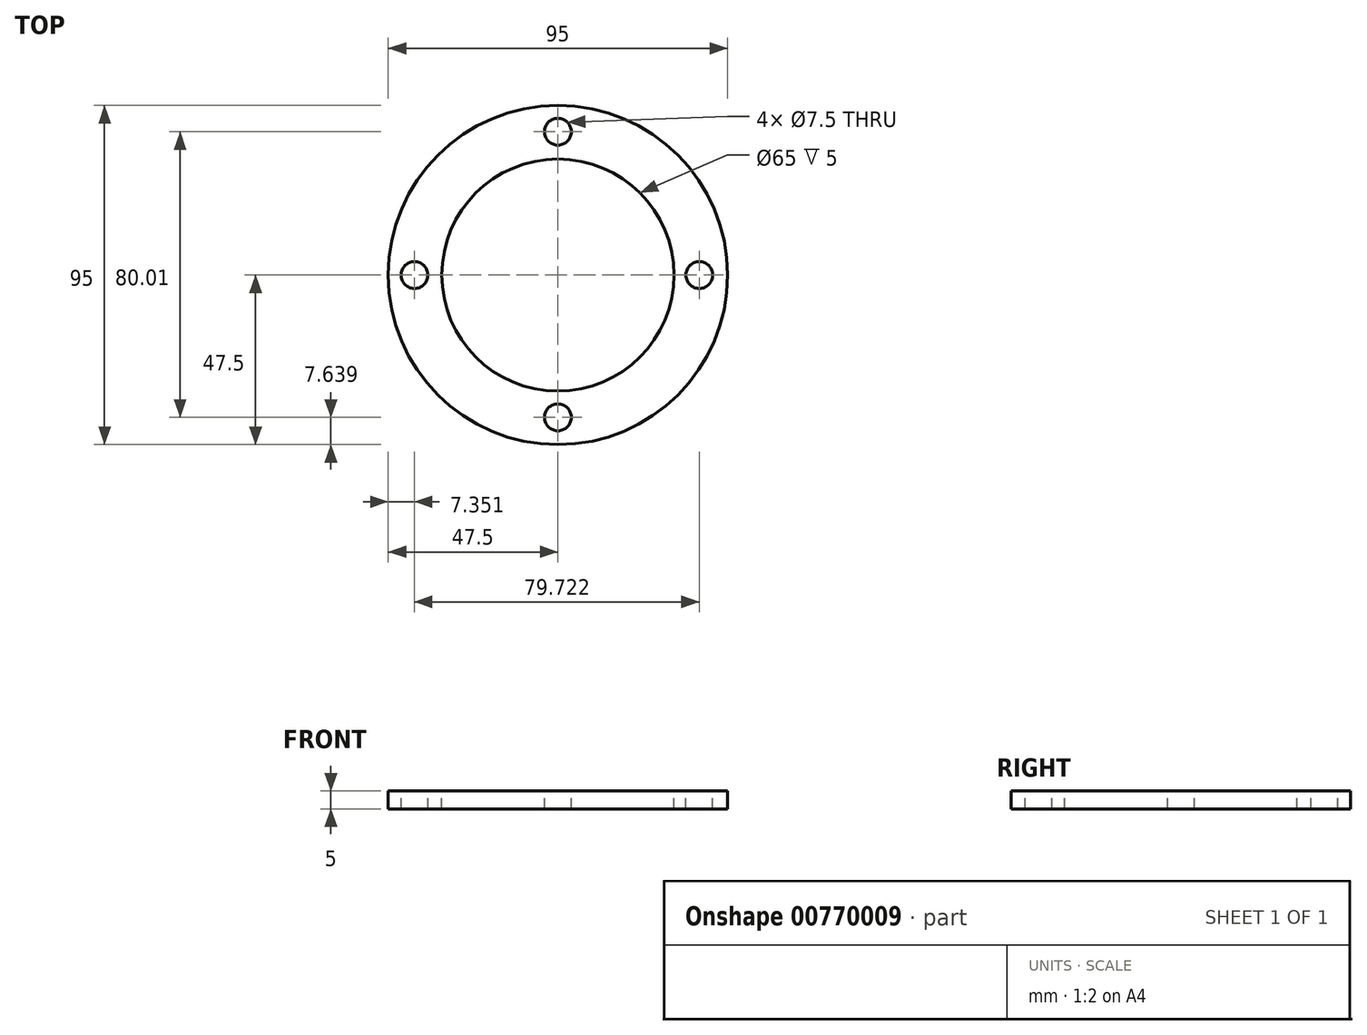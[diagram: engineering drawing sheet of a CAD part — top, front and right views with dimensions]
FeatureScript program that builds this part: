
annotation { "Feature Type Name" : "Feature", "Feature Type Description" : "" }
export const myFeature = defineFeature(function(context is Context, id is Id, definition is map)
    precondition{}
    {
        {
            var Q0;
            Q0=qCreatedBy(makeId("Top.planeOp"),FACE);
            var sketch = newSketch(context, id + "F0", { "sketchPlane" : qUnion([Q0])});
            skCircle(sketch, "E0", {"center": v(0, 0) * mm, "radius": 32.5 * mm});
            skCircle(sketch, "E1", {"center": v(0, 0) * mm, "radius": 47.5 * mm});
            skCircle(sketch, "E2", {"center": v(-40.15, 0) * mm, "radius": 3 * mm});
            skCircle(sketch, "E3", {"center": v(39.57, 0) * mm, "radius": 3 * mm});
            skCircle(sketch, "E4", {"center": v(0, 40.15) * mm, "radius": 3 * mm});
            skCircle(sketch, "E5", {"center": v(0, -39.86) * mm, "radius": 3 * mm});
            skCircle(sketch, "E6", {"center": v(0, -39.86) * mm, "radius": 3.75 * mm});
            skCircle(sketch, "E7", {"center": v(39.57, 0) * mm, "radius": 3.75 * mm});
            skCircle(sketch, "E8", {"center": v(0, 40.15) * mm, "radius": 3.75 * mm});
            skCircle(sketch, "E9", {"center": v(-40.15, 0) * mm, "radius": 3.75 * mm});
            skSolve(sketch);
        }
        {
            var Q0;
            Q0=makeQuery(id+"F0.imprint","IMPRINT",FACE,{"disambiguationData":[TD([[makeQuery(id+"F0.imprint","IMPRINT",EDGE,{"derivedFrom":sQuery(id+"F0.wireOp",EDGE,"E0")}),-1.0]])]});
            extrude(context, id + "F1", {"entities" : qUnion([Q0]), "oppositeDirection" : true, "depth" : 5 * mm, "offsetDistance" : 25 * mm});
        }
    });
